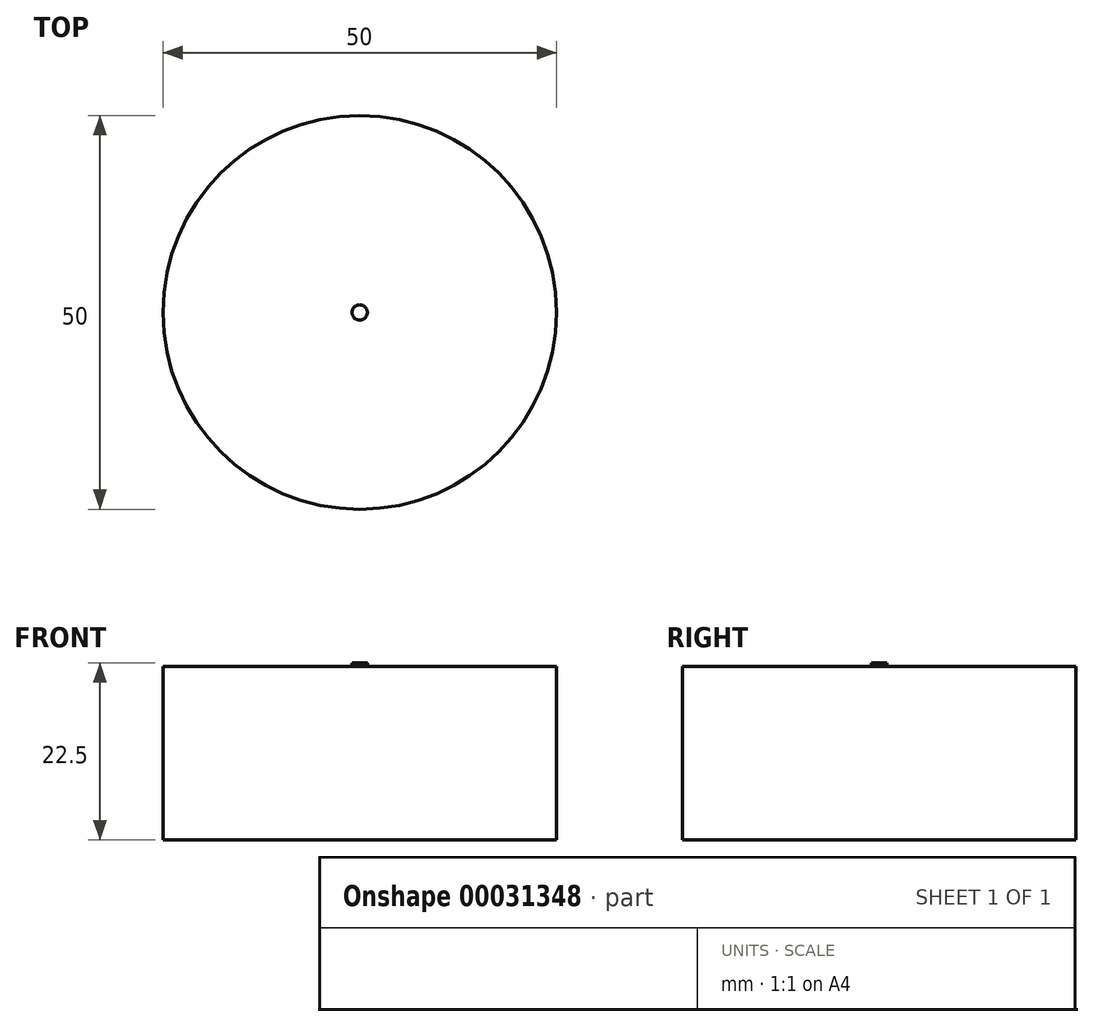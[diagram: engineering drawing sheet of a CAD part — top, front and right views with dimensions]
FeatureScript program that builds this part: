
annotation { "Feature Type Name" : "Feature", "Feature Type Description" : "" }
export const myFeature = defineFeature(function(context is Context, id is Id, definition is map)
    precondition{}
    {
        {
            var Q0;
            Q0=qCreatedBy(makeId("Top.planeOp"),FACE);
            var sketch = newSketch(context, id + "F0", { "sketchPlane" : qUnion([Q0])});
            skCircle(sketch, "E0", {"center": v(0, 0) * mm, "radius": 25 * mm});
            skSolve(sketch);
        }
        {
            var Q0;
            Q0 = qSketchRegion(id + "F0", true);
            extrude(context, id + "F1", {"entities" : qUnion([Q0]), "endBound" : BoundingType.SYMMETRIC, "depth" : 22 * mm});
        }
        {
            var Q0;
            Q0=makeQuery(id+"F1.opExtrude","CAP_FACE",FACE,{"disambiguationData":[OSD([sQuery(id+"F0.wireOp",EDGE,"E0")])],"isStart":false});
            var sketch = newSketch(context, id + "F2", { "sketchPlane" : qUnion([Q0])});
            skCircle(sketch, "E1", {"center": v(0, 0) * mm, "radius": 0.97 * mm});
            skSolve(sketch);
        }
        {
            var Q0;
            Q0 = qSketchRegion(id + "F2", true);
            extrude(context, id + "F3", {"entities" : qUnion([Q0]), "operationType" : NewBodyOperationType.ADD, "depth" : 0.5 * mm});
        }
    });
